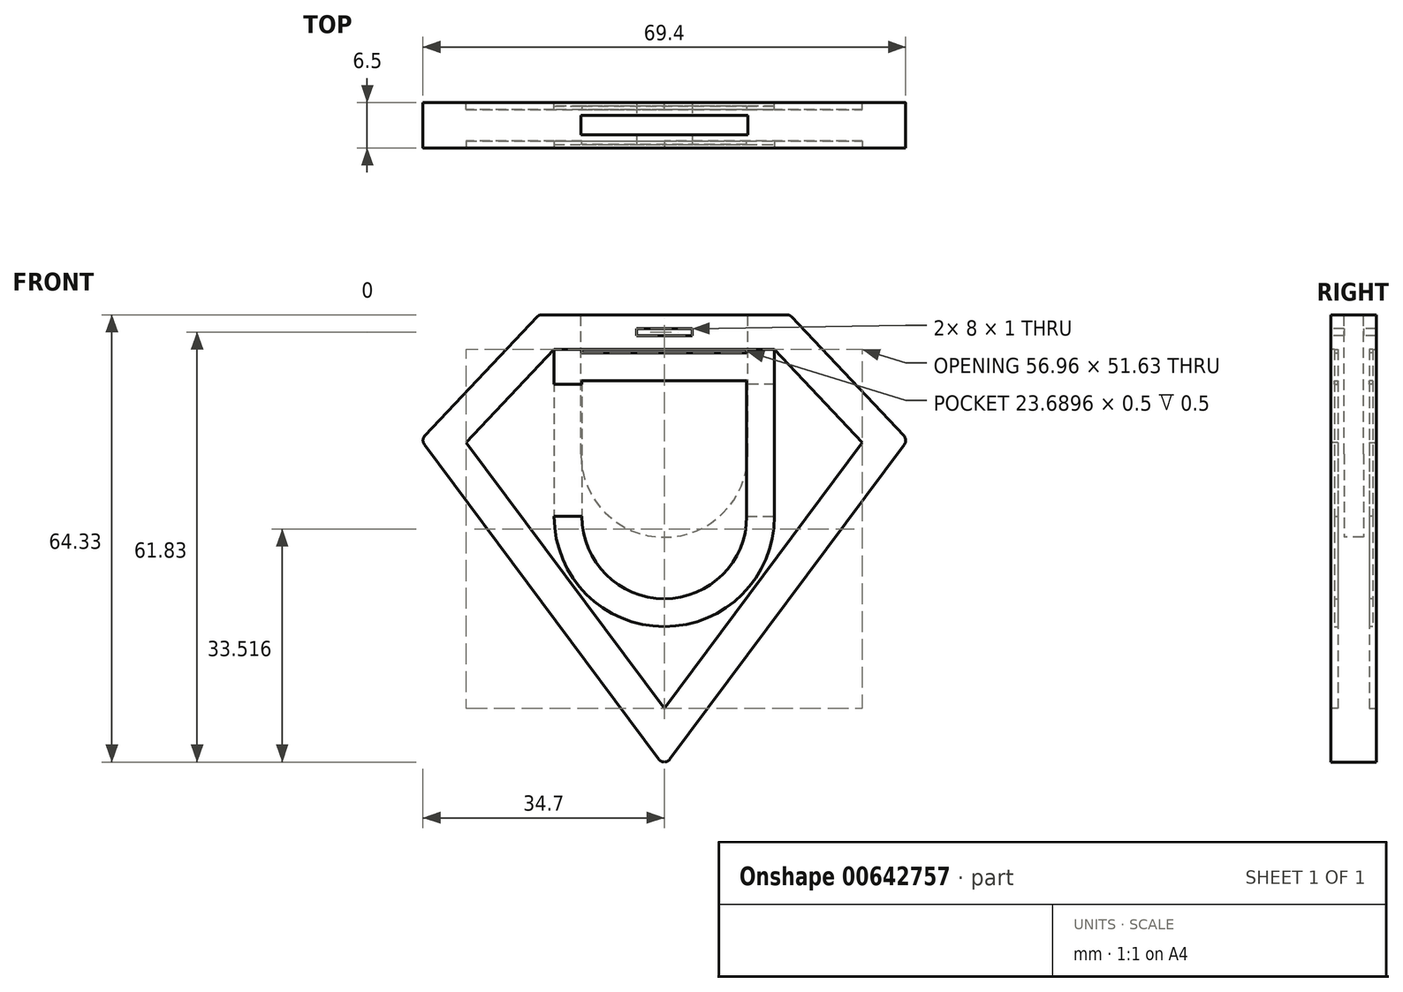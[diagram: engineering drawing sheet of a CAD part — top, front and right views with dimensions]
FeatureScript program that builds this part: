
annotation { "Feature Type Name" : "Feature", "Feature Type Description" : "" }
export const myFeature = defineFeature(function(context is Context, id is Id, definition is map)
    precondition{}
    {
        {
            var Q0;
            Q0=qCreatedBy(makeId("Front.planeOp"),FACE);
            var sketch = newSketch(context, id + "F0", { "sketchPlane" : qUnion([Q0])});
            skLineSegment(sketch, "E0", {"start": v(0, 18) * mm, "end": v(18, 18) * mm});
            skLineSegment(sketch, "E1", {"start": v(18, 18) * mm, "end": v(35, 0) * mm});
            skLineSegment(sketch, "E2", {"start": v(35, 0) * mm, "end": v(0, -47) * mm});
            skLineSegment(sketch, "E3", {"start": v(0, 18) * mm, "end": v(0, -47) * mm, "construction": true});
            skLineSegment(sketch, "E4.MirrorCS", {"start": v(-35, 0) * mm, "end": v(0, -47) * mm});
            skLineSegment(sketch, "E5.MirrorCS", {"start": v(-18, 18) * mm, "end": v(-35, 0) * mm});
            skLineSegment(sketch, "E6.MirrorCS", {"start": v(0, 18) * mm, "end": v(-18, 18) * mm});
            skSolve(sketch);
        }
        {
            var Q0;
            Q0=qSketchRegion(id+"F0",true);
            extrude(context, id + "F1", {"entities" : qUnion([Q0]), "endBound" : BoundingType.SYMMETRIC, "depth" : 6.5 * mm, "offsetDistance" : 25 * mm});
        }
        {
            var Q0;
            Q0=makeQuery(id+"F1.opExtrude","CAP_FACE",FACE,{"disambiguationData":[OSD([sQuery(id+"F0.wireOp",EDGE,"E0"),sQuery(id+"F0.wireOp",EDGE,"E1"),sQuery(id+"F0.wireOp",EDGE,"E2"),sQuery(id+"F0.wireOp",EDGE,"E4.MirrorCS"),sQuery(id+"F0.wireOp",EDGE,"E5.MirrorCS"),sQuery(id+"F0.wireOp",EDGE,"E6.MirrorCS")])],"isStart":false});
            var sketch = newSketch(context, id + "F2", { "sketchPlane" : qUnion([Q0])});
            skLineSegment(sketch, "E7.0", {"start": v(-15.84, 13) * mm, "end": v(15.84, 13) * mm});
            skLineSegment(sketch, "E8.0", {"start": v(-15.84, 13) * mm, "end": v(-28.48, -0.38) * mm});
            skLineSegment(sketch, "E9.0", {"start": v(-28.48, -0.38) * mm, "end": v(0, -38.63) * mm});
            skLineSegment(sketch, "E10.0", {"start": v(28.48, -0.38) * mm, "end": v(0, -38.63) * mm});
            skLineSegment(sketch, "E11.0", {"start": v(15.84, 13) * mm, "end": v(28.48, -0.38) * mm});
            skSolve(sketch);
        }
        {
            var Q0;
            Q0=qSketchRegion(id+"F2",true);
            extrude(context, id + "F3", {"entities" : qUnion([Q0]), "operationType" : NewBodyOperationType.REMOVE, "oppositeDirection" : true, "depth" : 1 * mm, "offsetDistance" : 25 * mm});
        }
        {
            var Q0;
            Q0=makeQuery(id+"F1.opExtrude","CAP_FACE",FACE,{"disambiguationData":[OSD([sQuery(id+"F0.wireOp",EDGE,"E0"),sQuery(id+"F0.wireOp",EDGE,"E1"),sQuery(id+"F0.wireOp",EDGE,"E2"),sQuery(id+"F0.wireOp",EDGE,"E4.MirrorCS"),sQuery(id+"F0.wireOp",EDGE,"E5.MirrorCS"),sQuery(id+"F0.wireOp",EDGE,"E6.MirrorCS")])],"isStart":true});
            var sketch = newSketch(context, id + "F4", { "sketchPlane" : qUnion([Q0])});
            skLineSegment(sketch, "E12.0", {"start": v(15.84, 13) * mm, "end": v(-15.84, 13) * mm});
            skLineSegment(sketch, "E13.0", {"start": v(15.84, 13) * mm, "end": v(28.48, -0.38) * mm});
            skLineSegment(sketch, "E14.0", {"start": v(28.48, -0.38) * mm, "end": v(0, -38.63) * mm});
            skLineSegment(sketch, "E15.0", {"start": v(-28.48, -0.38) * mm, "end": v(0, -38.63) * mm});
            skLineSegment(sketch, "E15.1", {"start": v(-15.84, 13) * mm, "end": v(-28.48, -0.38) * mm});
            skSolve(sketch);
        }
        {
            var Q0;
            Q0=qSketchRegion(id+"F4",true);
            extrude(context, id + "F5", {"entities" : qUnion([Q0]), "operationType" : NewBodyOperationType.REMOVE, "oppositeDirection" : true, "depth" : 1 * mm, "offsetDistance" : 25 * mm});
        }
        {
            var Q0;
            Q0=makeQuery(id+"F3.boolean.opBoolean","COPY",FACE,{"derivedFrom":makeQuery(id+"F3.opExtrude","CAP_FACE",FACE,{"disambiguationData":[OSD([sQuery(id+"F2.wireOp",EDGE,"E7.0"),sQuery(id+"F2.wireOp",EDGE,"E8.0"),sQuery(id+"F2.wireOp",EDGE,"E9.0"),sQuery(id+"F2.wireOp",EDGE,"E10.0"),sQuery(id+"F2.wireOp",EDGE,"E11.0")])],"isStart":false})});
            var sketch = newSketch(context, id + "F6", { "sketchPlane" : qUnion([Q0])});
            skLineSegment(sketch, "E16", {"start": v(11.84, 13) * mm, "end": v(11.84, 12.5) * mm});
            skLineSegment(sketch, "E17", {"start": v(11.84, 12.5) * mm, "end": v(-11.84, 12.5) * mm});
            skLineSegment(sketch, "E18", {"start": v(-11.84, 13) * mm, "end": v(-15.84, 13) * mm});
            skLineSegment(sketch, "E19", {"start": v(0, 18) * mm, "end": v(0, -47.01) * mm, "construction": true});
            skLineSegment(sketch, "E20.MirrorCS", {"start": v(-11.84, 8) * mm, "end": v(-11.84, 8.5) * mm});
            skLineSegment(sketch, "E21.MirrorCS", {"start": v(-11.84, 13) * mm, "end": v(-11.84, 12.5) * mm});
            skLineSegment(sketch, "E22.MirrorCS", {"start": v(-15.84, 8) * mm, "end": v(-11.84, 8) * mm});
            skLineSegment(sketch, "E23.MirrorCS", {"start": v(11.84, 13) * mm, "end": v(15.84, 13) * mm});
            skLineSegment(sketch, "E24.MirrorCS", {"start": v(-11.84, -11) * mm, "end": v(-15.84, -11) * mm});
            skLineSegment(sketch, "E25.MirrorCS", {"start": v(-15.84, 13) * mm, "end": v(-15.84, 8) * mm});
            skLineSegment(sketch, "E26.MirrorCS", {"start": v(11.84, 8.5) * mm, "end": v(11.84, -11) * mm});
            skLineSegment(sketch, "E27.MirrorCS", {"start": v(15.84, 13) * mm, "end": v(15.84, -11) * mm});
            skArc(sketch, "E28.MirrorCS", {"start": v(11.84, -11) * mm, "mid": v(0, -22.84) * mm, "end": v(-11.84, -11) * mm});
            skLineSegment(sketch, "E29.MirrorCS", {"start": v(-11.84, 8.5) * mm, "end": v(11.84, 8.5) * mm});
            skLineSegment(sketch, "E30.MirrorCS", {"start": v(-11.84, 12.5) * mm, "end": v(11.84, 12.5) * mm});
            skArc(sketch, "E31.MirrorCS", {"start": v(15.84, -11) * mm, "mid": v(0, -26.84) * mm, "end": v(-15.84, -11) * mm});
            skSolve(sketch);
        }
        {
            var Q0;
            Q0=qSketchRegion(id+"F6",true);
            extrude(context, id + "F7", {"entities" : qUnion([Q0]), "operationType" : NewBodyOperationType.ADD, "depth" : 0.5 * mm, "offsetDistance" : 25 * mm});
        }
        {
            var Q0;
            Q0=makeQuery(id+"F5.boolean.opBoolean","COPY",FACE,{"derivedFrom":makeQuery(id+"F5.opExtrude","CAP_FACE",FACE,{"disambiguationData":[OSD([sQuery(id+"F4.wireOp",EDGE,"E12.0"),sQuery(id+"F4.wireOp",EDGE,"E13.0"),sQuery(id+"F4.wireOp",EDGE,"E14.0"),sQuery(id+"F4.wireOp",EDGE,"E15.0"),sQuery(id+"F4.wireOp",EDGE,"E15.1")])],"isStart":false})});
            var sketch = newSketch(context, id + "F8", { "sketchPlane" : qUnion([Q0])});
            skLineSegment(sketch, "E32", {"start": v(11.84, 13) * mm, "end": v(11.84, 12.5) * mm});
            skLineSegment(sketch, "E33", {"start": v(11.84, 12.5) * mm, "end": v(-11.84, 12.5) * mm});
            skLineSegment(sketch, "E34", {"start": v(-11.84, 13) * mm, "end": v(-15.84, 13) * mm});
            skLineSegment(sketch, "E35", {"start": v(0, 18) * mm, "end": v(0, -47.01) * mm, "construction": true});
            skLineSegment(sketch, "E36.MirrorCS", {"start": v(-11.84, 8) * mm, "end": v(-11.84, 8.5) * mm});
            skLineSegment(sketch, "E37.MirrorCS", {"start": v(-11.84, 13) * mm, "end": v(-11.84, 12.5) * mm});
            skLineSegment(sketch, "E38.MirrorCS", {"start": v(-15.84, 8) * mm, "end": v(-11.84, 8) * mm});
            skLineSegment(sketch, "E39.MirrorCS", {"start": v(11.84, 13) * mm, "end": v(15.84, 13) * mm});
            skLineSegment(sketch, "E40.MirrorCS", {"start": v(-11.84, -11) * mm, "end": v(-15.84, -11) * mm});
            skLineSegment(sketch, "E41.MirrorCS", {"start": v(-15.84, 13) * mm, "end": v(-15.84, 8) * mm});
            skLineSegment(sketch, "E42.MirrorCS", {"start": v(11.84, 8.5) * mm, "end": v(11.84, -11) * mm});
            skLineSegment(sketch, "E43.MirrorCS", {"start": v(15.84, 13) * mm, "end": v(15.84, -11) * mm});
            skArc(sketch, "E44.MirrorCS", {"start": v(11.84, -11) * mm, "mid": v(0, -22.84) * mm, "end": v(-11.84, -11) * mm});
            skLineSegment(sketch, "E45.MirrorCS", {"start": v(-11.84, 8.5) * mm, "end": v(11.84, 8.5) * mm});
            skLineSegment(sketch, "E46.MirrorCS", {"start": v(-11.84, 12.5) * mm, "end": v(11.84, 12.5) * mm});
            skArc(sketch, "E47.MirrorCS", {"start": v(15.84, -11) * mm, "mid": v(0, -26.84) * mm, "end": v(-15.84, -11) * mm});
            skSolve(sketch);
        }
        {
            var Q0;
            Q0=qSketchRegion(id+"F8",true);
            extrude(context, id + "F9", {"entities" : qUnion([Q0]), "operationType" : NewBodyOperationType.ADD, "depth" : 0.5 * mm, "offsetDistance" : 25 * mm});
        }
        {
            var Q0;
            Q0=makeQuery(id+"F1.opExtrude","SWEPT_FACE",FACE,{"disambiguationData":[OSD([sQuery(id+"F0.wireOp",EDGE,"E0"),sQuery(id+"F0.wireOp",EDGE,"E6.MirrorCS")])]});
            var sketch = newSketch(context, id + "F10", { "sketchPlane" : qUnion([Q0])});
            skLineSegment(sketch, "E48.bottom", {"start": v(-12, 1.4) * mm, "end": v(12, 1.4) * mm});
            skLineSegment(sketch, "E48.top", {"start": v(-12, -1.4) * mm, "end": v(12, -1.4) * mm});
            skLineSegment(sketch, "E48.left", {"start": v(-12, 1.4) * mm, "end": v(-12, -1.4) * mm});
            skLineSegment(sketch, "E48.right", {"start": v(12, 1.4) * mm, "end": v(12, -1.4) * mm});
            skSolve(sketch);
        }
        {
            var Q0;
            Q0=qSketchRegion(id+"F10",true);
            extrude(context, id + "F11", {"entities" : qUnion([Q0]), "operationType" : NewBodyOperationType.REMOVE, "oppositeDirection" : true, "depth" : 20 * mm, "offsetDistance" : 25 * mm});
        }
        {
            var Q0;
            Q0=qCreatedBy(makeId("Front.planeOp"),FACE);
            var sketch = newSketch(context, id + "F12", { "sketchPlane" : qUnion([Q0])});
            skLineSegment(sketch, "E49.0", {"start": v(-12, -2) * mm, "end": v(12, -2) * mm});
            skArc(sketch, "E50", {"start": v(-12, -2) * mm, "mid": v(0, -14) * mm, "end": v(12, -2) * mm});
            skSolve(sketch);
        }
        {
            var Q0;
            Q0=qSketchRegion(id+"F12",true);
            extrude(context, id + "F13", {"entities" : qUnion([Q0]), "operationType" : NewBodyOperationType.REMOVE, "endBound" : BoundingType.SYMMETRIC, "oppositeDirection" : true, "depth" : 2.8 * mm, "offsetDistance" : 25 * mm});
        }
        {
            var Q0;
            Q0=makeQuery(id+"F1.opExtrude","CAP_FACE",FACE,{"disambiguationData":[OSD([sQuery(id+"F0.wireOp",EDGE,"E0"),sQuery(id+"F0.wireOp",EDGE,"E1"),sQuery(id+"F0.wireOp",EDGE,"E2"),sQuery(id+"F0.wireOp",EDGE,"E4.MirrorCS"),sQuery(id+"F0.wireOp",EDGE,"E5.MirrorCS"),sQuery(id+"F0.wireOp",EDGE,"E6.MirrorCS")])],"isStart":false});
            var sketch = newSketch(context, id + "F14", { "sketchPlane" : qUnion([Q0])});
            skLineSegment(sketch, "E51.bottom", {"start": v(-4, 16) * mm, "end": v(4, 16) * mm});
            skLineSegment(sketch, "E51.top", {"start": v(-4, 15) * mm, "end": v(4, 15) * mm});
            skLineSegment(sketch, "E51.left", {"start": v(-4, 16) * mm, "end": v(-4, 15) * mm});
            skLineSegment(sketch, "E51.right", {"start": v(4, 16) * mm, "end": v(4, 15) * mm});
            skSolve(sketch);
        }
        {
            var Q0;
            Q0=qSketchRegion(id+"F14",true);
            extrude(context, id + "F15", {"entities" : qUnion([Q0]), "operationType" : NewBodyOperationType.REMOVE, "oppositeDirection" : true, "depth" : 25 * mm, "offsetDistance" : 25 * mm});
        }
        {
            var Q0;
            Q0=makeQuery(id+"F1.opExtrude","SWEPT_EDGE",EDGE,{"disambiguationData":[OSD([sQuery(id+"F0.wireOp",EDGE,"E2"),sQuery(id+"F0.wireOp",EDGE,"E4.MirrorCS")])]});
            var Q1;
            Q1=makeQuery(id+"F1.opExtrude","SWEPT_EDGE",EDGE,{"disambiguationData":[OSD([sQuery(id+"F0.wireOp",EDGE,"E1"),sQuery(id+"F0.wireOp",EDGE,"E2")])]});
            var Q2;
            Q2=makeQuery(id+"F1.opExtrude","SWEPT_EDGE",EDGE,{"disambiguationData":[OSD([sQuery(id+"F0.wireOp",EDGE,"E4.MirrorCS"),sQuery(id+"F0.wireOp",EDGE,"E5.MirrorCS")])]});
            var Q3;
            Q3=makeQuery(id+"F1.opExtrude","SWEPT_EDGE",EDGE,{"disambiguationData":[OSD([sQuery(id+"F0.wireOp",EDGE,"E5.MirrorCS"),sQuery(id+"F0.wireOp",EDGE,"E6.MirrorCS")])]});
            var Q4;
            Q4=makeQuery(id+"F1.opExtrude","SWEPT_EDGE",EDGE,{"disambiguationData":[OSD([sQuery(id+"F0.wireOp",EDGE,"E0"),sQuery(id+"F0.wireOp",EDGE,"E1")])]});
            fillet(context, id + "F16", {"entities" : qUnion([Q0, Q1, Q2, Q3, Q4]), "radius" : 1 * mm, "tangentPropagation" : true, "allowEdgeOverflow" : false});
        }
    });
